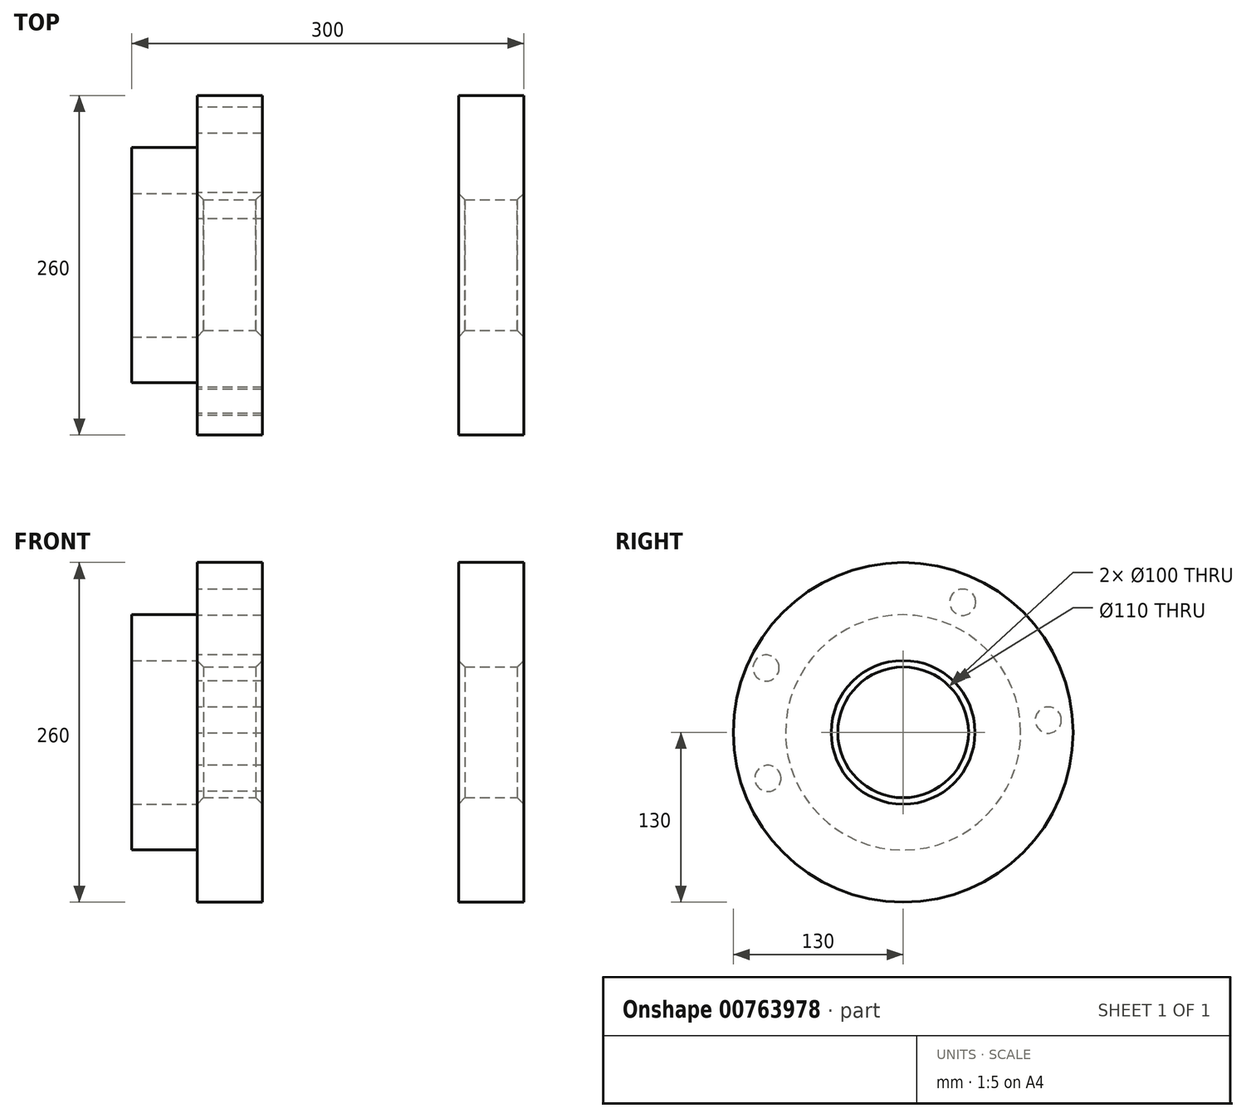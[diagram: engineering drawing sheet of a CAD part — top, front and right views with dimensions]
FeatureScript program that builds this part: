
annotation { "Feature Type Name" : "Feature", "Feature Type Description" : "" }
export const myFeature = defineFeature(function(context is Context, id is Id, definition is map)
    precondition{}
    {
        {
            var Q0;
            Q0=qCreatedBy(makeId("Front.planeOp"),FACE);
            var sketch = newSketch(context, id + "F0", { "sketchPlane" : qUnion([Q0])});
            skLineSegment(sketch, "E0.bottom", {"start": v(-50, 150) * mm, "end": v(0, 150) * mm});
            skLineSegment(sketch, "E0.top", {"start": v(-50, 50) * mm, "end": v(0, 50) * mm});
            skLineSegment(sketch, "E0.left", {"start": v(-50, 150) * mm, "end": v(-50, 50) * mm});
            skLineSegment(sketch, "E0.right", {"start": v(0, 150) * mm, "end": v(0, 50) * mm});
            skLineSegment(sketch, "E1", {"start": v(0, 0) * mm, "end": v(-34.97, 0) * mm});
            skSolve(sketch);
        }
        {
            var Q0;
            Q0=makeQuery(id+"F0.imprint","IMPRINT",FACE,{"disambiguationData":[TD([[makeQuery(id+"F0.imprint","IMPRINT",EDGE,{"derivedFrom":sQuery(id+"F0.wireOp",EDGE,"E0.bottom")}),-1.0]])]});
            var Q1;
            Q1=sQuery(id+"F0.wireOp",EDGE,"E1");
            revolve(context, id + "F1", {"surfaceOperationType" : NewSurfaceOperationType.NEW, "entities" : qUnion([Q0]), "axis" : qUnion([Q1]), "revolveType" : RevolveType.FULL});
        }
        {
            var Q0;
            Q0=makeQuery(id+"F1.opRevolve","SWEPT_FACE",FACE,{"disambiguationData":[OSD([sQuery(id+"F0.wireOp",EDGE,"E0.top")])]});
            chamfer(context, id + "F2", {"entities" : qUnion([Q0]), "width" : 5 * mm, "tangentPropagation" : true});
        }
        {
            var Q0;
            Q0=makeQuery(id+"F1.opRevolve","SWEPT_FACE",FACE,{"disambiguationData":[OSD([sQuery(id+"F0.wireOp",EDGE,"E0.bottom")])]});
            fillet(context, id + "F3", {"entities" : qUnion([Q0]), "radius" : 5 * mm, "tangentPropagation" : true, "allowEdgeOverflow" : false});
        }
        {
            var Q0;
            Q0=makeQuery(id+"F1.opRevolve","SWEPT_BODY",BODY,{"disambiguationData":[OSD([sQuery(id+"F0.wireOp",EDGE,"E0.bottom"),sQuery(id+"F0.wireOp",EDGE,"E0.top"),sQuery(id+"F0.wireOp",EDGE,"E0.left"),sQuery(id+"F0.wireOp",EDGE,"E0.right")])]});
            var Q1;
            Q1=sQuery(id+"F0.wireOp",EDGE,"E1");
            transform(context, id + "F4", {"entities" : qUnion([Q0]), "transformType" : TransformType.TRANSLATION_DISTANCE, "transformDirection" : qUnion([Q1]), "distance" : 200 * mm, "makeCopy" : true});
        }
        {
            var Q0;
            Q0=makeQuery(id+"F4.opPattern","COPY",FACE,{"derivedFrom":makeQuery(id+"F1.opRevolve","SWEPT_FACE",FACE,{"disambiguationData":[OSD([sQuery(id+"F0.wireOp",EDGE,"E0.left")])]}),"instanceName":"1"});
            var sketch = newSketch(context, id + "F5", { "sketchPlane" : qUnion([Q0])});
            skCircle(sketch, "E2.0", {"center": v(0, 0) * mm, "radius": 50 * mm});
            skCircle(sketch, "E3", {"center": v(0, 0) * mm, "radius": 90 * mm});
            skCircle(sketch, "E4", {"center": v(0, 0) * mm, "radius": 130 * mm});
            skCircle(sketch, "E5", {"center": v(0, 0) * mm, "radius": 175 * mm});
            skPoint(sketch, "E6", {"position": v(-45.57, 99.6) * mm});
            skPoint(sketch, "E7", {"position": v(-111.06, 9.43) * mm});
            skPoint(sketch, "E8", {"position": v(103.46, -35.18) * mm});
            skPoint(sketch, "E9", {"position": v(104.88, 49.3) * mm});
            skSolve(sketch);
        }
        {
            var Q0;
            Q0=makeQuery(id+"F5.imprint","IMPRINT",FACE,{"disambiguationData":[TD([[makeQuery(id+"F5.imprint","IMPRINT",EDGE,{"derivedFrom":sQuery(id+"F5.wireOp",EDGE,"E3")}),1.0]])]});
            extrude(context, id + "F6", {"entities" : qUnion([Q0]), "operationType" : NewBodyOperationType.ADD, "depth" : 50 * mm, "offsetDistance" : 25 * mm});
        }
        {
            var Q0;
            Q0=makeQuery(id+"F5.imprint","IMPRINT",FACE,{"disambiguationData":[TD([[makeQuery(id+"F5.imprint","IMPRINT",EDGE,{"derivedFrom":sQuery(id+"F5.wireOp",EDGE,"E5")}),1.0]])]});
            var Q1;
            Q1=makeQuery(id+"F5.imprint","IMPRINT",FACE,{"disambiguationData":[TD([[makeQuery(id+"F5.imprint","IMPRINT",EDGE,{"derivedFrom":sQuery(id+"F5.wireOp",EDGE,"E4")}),-1.0]])]});
            extrude(context, id + "F7", {"entities" : qUnion([Q0, Q1]), "operationType" : NewBodyOperationType.REMOVE, "endBound" : BoundingType.THROUGH_ALL, "oppositeDirection" : true, "depth" : 25 * mm, "offsetDistance" : 25 * mm});
        }
        {
            var Q0;
            Q0=sQuery(id+"F5.wireOp",VERTEX,"E6");
            var Q1;
            Q1=sQuery(id+"F5.wireOp",VERTEX,"E7");
            var Q2;
            Q2=sQuery(id+"F5.wireOp",VERTEX,"E9");
            var Q3;
            Q3=sQuery(id+"F5.wireOp",VERTEX,"E8");
            var Q4;
            Q4=makeQuery(id+"F4.opPattern","COPY",BODY,{"derivedFrom":makeQuery(id+"F1.opRevolve","SWEPT_BODY",BODY,{"disambiguationData":[OSD([sQuery(id+"F0.wireOp",EDGE,"E0.bottom"),sQuery(id+"F0.wireOp",EDGE,"E0.top"),sQuery(id+"F0.wireOp",EDGE,"E0.left"),sQuery(id+"F0.wireOp",EDGE,"E0.right")])]}),"instanceName":"1"});
            hole(context, id + "F8", {"style" : HoleStyle.SIMPLE, "endStyle" : HoleEndStyle.THROUGH, "holeDiameter" : 20 * mm, "majorDiameter" : 5 * mm, "isTappedThrough" : true, "tappedDepth" : 20 * mm, "tapClearance" : 4, "locations" : qUnion([Q0, Q1, Q2, Q3]), "scope" : qUnion([Q4])});
        }
    });
